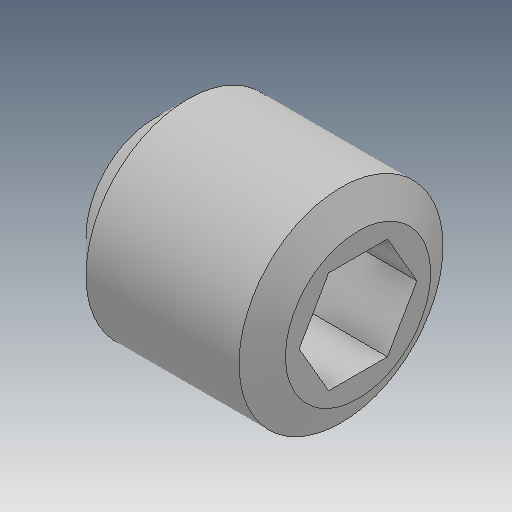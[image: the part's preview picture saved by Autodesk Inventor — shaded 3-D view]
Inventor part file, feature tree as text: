
AUTODESK INVENTOR PART (.ipt)
format: ipt  version: 2019 (Build 230136000, 136)  size: 117,760 bytes
history: native  units: mm
features: chamfer x1
ambient origin geometry x8: Origin, YZ Plane, XZ Plane, XY Plane, X Axis, Y Axis, Z Axis, Center Point
bodies: Solid1 (feature_tree)
feature tree (1):
  chamfer  "Fase1"  [1 undecoded]
note: 1 required parameter value undecoded (feature->parameter linkage not recoverable at this tier; creation-order binding heuristic only, values carry confidence <= 0.55)
